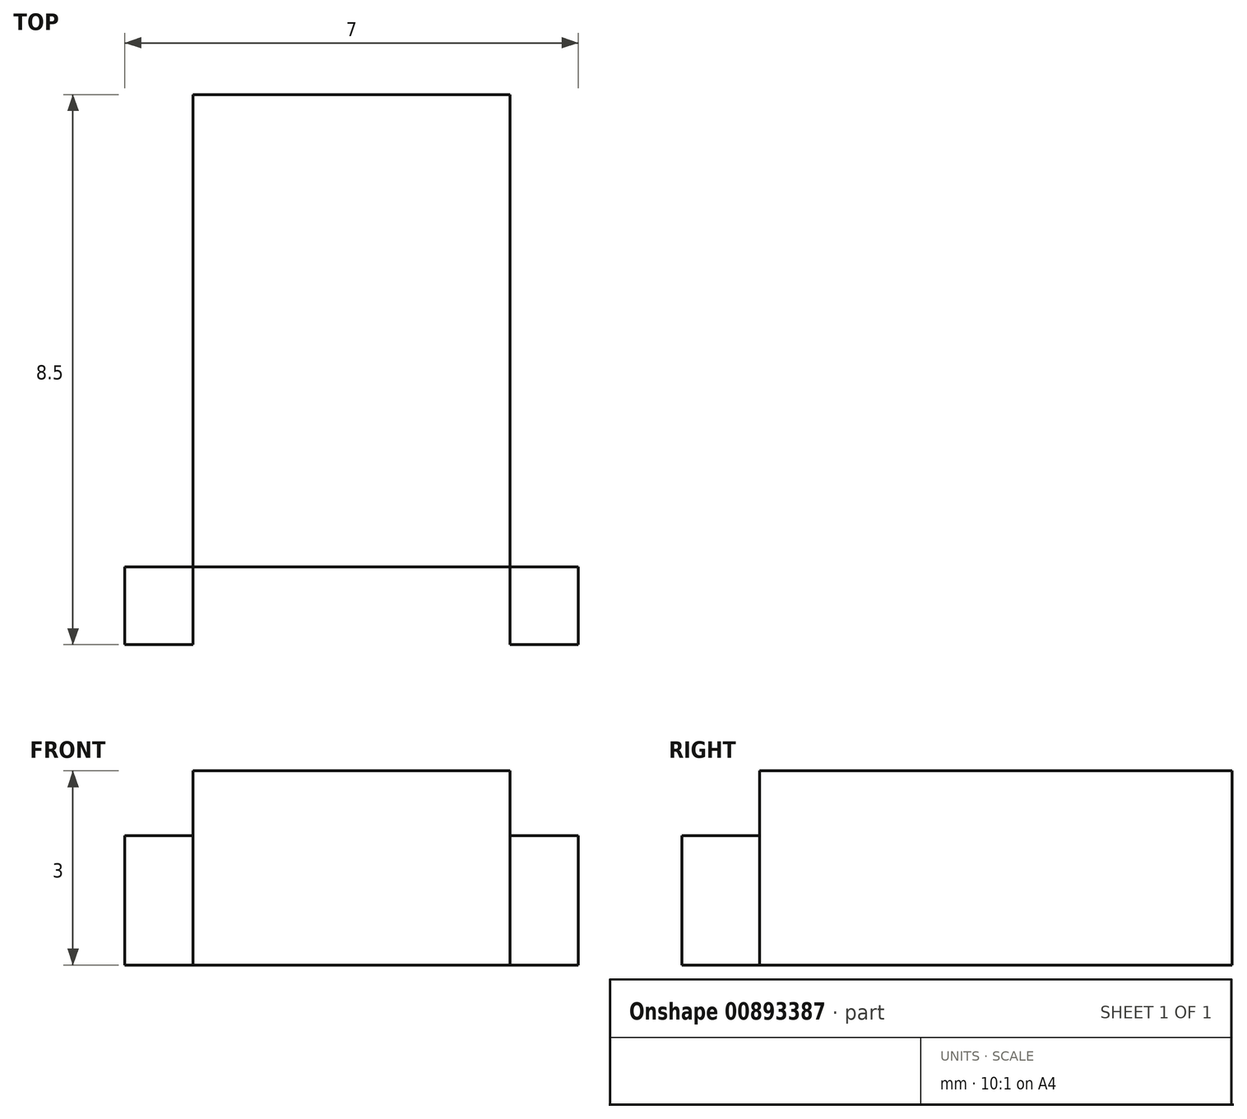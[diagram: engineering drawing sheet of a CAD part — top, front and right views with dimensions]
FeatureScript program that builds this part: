
annotation { "Feature Type Name" : "Feature", "Feature Type Description" : "" }
export const myFeature = defineFeature(function(context is Context, id is Id, definition is map)
    precondition{}
    {
        {
            var Q0;
            Q0=qCreatedBy(makeId("Front.planeOp"),FACE);
            var sketch = newSketch(context, id + "F0", { "sketchPlane" : qUnion([Q0])});
            skLineSegment(sketch, "E0.bottom", {"start": v(-2.45, 0) * mm, "end": v(2.45, 0) * mm});
            skLineSegment(sketch, "E0.top", {"start": v(-2.45, -3) * mm, "end": v(2.45, -3) * mm});
            skLineSegment(sketch, "E0.left", {"start": v(-2.45, 0) * mm, "end": v(-2.45, -3) * mm});
            skLineSegment(sketch, "E0.right", {"start": v(2.45, 0) * mm, "end": v(2.45, -3) * mm});
            skPoint(sketch, "E0.middle", {"position": v(0, -1.5) * mm});
            skSolve(sketch);
        }
        {
            var Q0;
            Q0=makeQuery(id+"F0.imprint","IMPRINT",FACE,{"disambiguationData":[TD([[makeQuery(id+"F0.imprint","IMPRINT",EDGE,{"derivedFrom":sQuery(id+"F0.wireOp",EDGE,"E0.bottom")}),-1.0]])]});
            extrude(context, id + "F1", {"entities" : qUnion([Q0]), "oppositeDirection" : true, "depth" : 7.3 * mm, "offsetDistance" : 25 * mm});
        }
        {
            var Q0;
            Q0=makeQuery(id+"F1.opExtrude","CAP_FACE",FACE,{"disambiguationData":[OSD([sQuery(id+"F0.wireOp",EDGE,"E0.bottom"),sQuery(id+"F0.wireOp",EDGE,"E0.top"),sQuery(id+"F0.wireOp",EDGE,"E0.left"),sQuery(id+"F0.wireOp",EDGE,"E0.right")])],"isStart":true});
            var sketch = newSketch(context, id + "F2", { "sketchPlane" : qUnion([Q0])});
            skLineSegment(sketch, "E1.bottom", {"start": v(-3.5, -1) * mm, "end": v(-2.45, -1) * mm});
            skLineSegment(sketch, "E1.top", {"start": v(-3.5, -3) * mm, "end": v(3.5, -3) * mm});
            skLineSegment(sketch, "E1.left", {"start": v(-3.5, -1) * mm, "end": v(-3.5, -3) * mm});
            skLineSegment(sketch, "E1.right", {"start": v(3.5, -1) * mm, "end": v(3.5, -3) * mm});
            skPoint(sketch, "E1.middle", {"position": v(0, -2) * mm});
            skLineSegment(sketch, "E2.0", {"start": v(-2.45, -3) * mm, "end": v(2.45, -3) * mm});
            skLineSegment(sketch, "E3.0", {"start": v(-2.45, 0) * mm, "end": v(-2.45, -1) * mm});
            skLineSegment(sketch, "E4.0", {"start": v(-2.45, 0) * mm, "end": v(2.45, 0) * mm});
            skLineSegment(sketch, "E5.0", {"start": v(2.45, 0) * mm, "end": v(2.45, -1) * mm});
            skLineSegment(sketch, "E6.trimOffspring", {"start": v(2.45, -1) * mm, "end": v(3.5, -1) * mm});
            skSolve(sketch);
        }
        {
            var Q0;
            {var subQ0=sQuery(id+"F2.wireOp",EDGE,"E1.right");Q0=makeQuery(id+"F2.imprint","IMPRINT",FACE,{"disambiguationData":[TD([[makeQuery(id+"F2.imprint","IMPRINT",EDGE,{"derivedFrom":subQ0}),-1.0]])]});}
            var Q1;
            {var subQ5=sQuery(id+"F2.wireOp",EDGE,"E2.0");Q1=makeQuery(id+"F2.imprint","IMPRINT",FACE,{"disambiguationData":[TD([[makeQuery(id+"F2.imprint","IMPRINT",EDGE,{"derivedFrom":subQ5}),1.0]])]});}
            var Q2;
            {var subQ0=sQuery(id+"F2.wireOp",EDGE,"E1.left");Q2=makeQuery(id+"F2.imprint","IMPRINT",FACE,{"disambiguationData":[TD([[makeQuery(id+"F2.imprint","IMPRINT",EDGE,{"derivedFrom":subQ0}),1.0]])]});}
            extrude(context, id + "F3", {"entities" : qUnion([Q0, Q1, Q2]), "operationType" : NewBodyOperationType.ADD, "depth" : 1.2 * mm, "offsetDistance" : 25 * mm});
        }
    });
